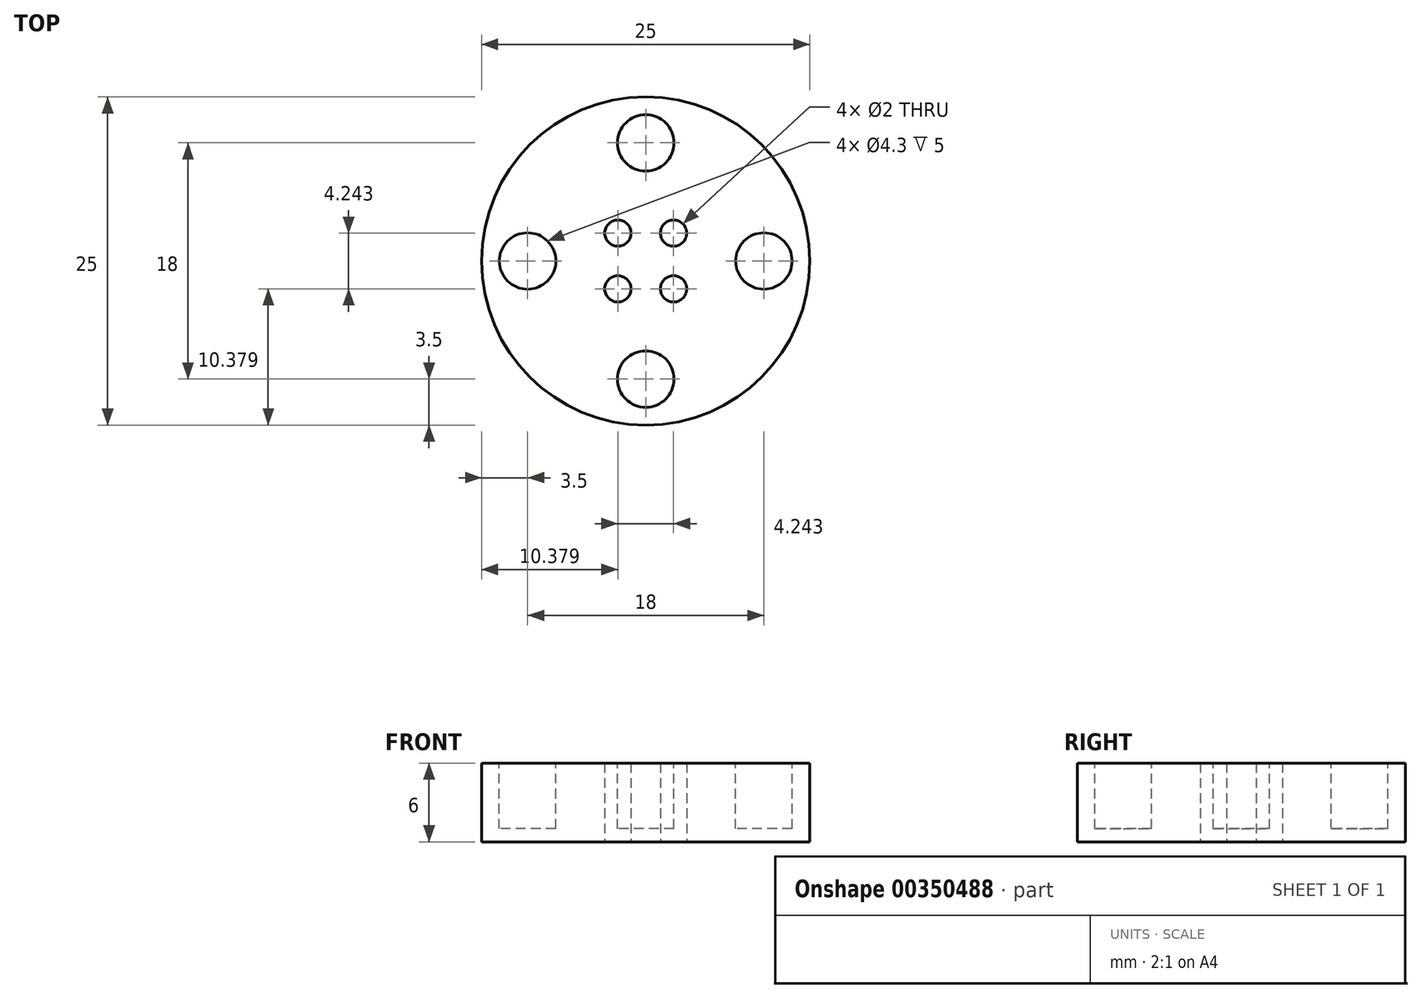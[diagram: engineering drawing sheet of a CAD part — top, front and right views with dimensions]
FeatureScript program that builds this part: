
annotation { "Feature Type Name" : "Feature", "Feature Type Description" : "" }
export const myFeature = defineFeature(function(context is Context, id is Id, definition is map)
    precondition{}
    {
        {
            var Q0;
            Q0=qCreatedBy(makeId("Top.planeOp"),FACE);
            var sketch = newSketch(context, id + "F0", { "sketchPlane" : qUnion([Q0])});
            skCircle(sketch, "E0", {"center": v(0, 0) * mm, "radius": 12.5 * mm});
            skCircle(sketch, "E1", {"center": v(2.12, 2.12) * mm, "radius": 1 * mm});
            skCircle(sketch, "E2.1.0", {"center": v(-2.12, 2.12) * mm, "radius": 1 * mm});
            skCircle(sketch, "E2.2.0", {"center": v(-2.12, -2.12) * mm, "radius": 1 * mm});
            skCircle(sketch, "E2.3.0", {"center": v(2.12, -2.12) * mm, "radius": 1 * mm});
            skSolve(sketch);
        }
        {
            var Q0;
            Q0 = qSketchRegion(id + "F0", true);
            extrude(context, id + "F1", {"entities" : qUnion([Q0]), "depth" : 6 * mm});
        }
        {
            var Q0;
            Q0=makeQuery(id+"F1.opExtrude","CAP_FACE",FACE,{"disambiguationData":[OSD([sQuery(id+"F0.wireOp",EDGE,"E0"),sQuery(id+"F0.wireOp",EDGE,"E1"),sQuery(id+"F0.wireOp",EDGE,"E2.1.0"),sQuery(id+"F0.wireOp",EDGE,"E2.2.0"),sQuery(id+"F0.wireOp",EDGE,"E2.3.0")])],"isStart":false});
            var sketch = newSketch(context, id + "F2", { "sketchPlane" : qUnion([Q0])});
            skLineSegment(sketch, "E3", {"start": v(0, 9) * mm, "end": v(0, 0) * mm});
            skLineSegment(sketch, "E4", {"start": v(0, 0) * mm, "end": v(10.37, 0) * mm});
            skCircle(sketch, "E5", {"center": v(0, 9) * mm, "radius": 2.15 * mm});
            skCircle(sketch, "E6.1.0", {"center": v(9, 0) * mm, "radius": 2.15 * mm});
            skCircle(sketch, "E6.2.0", {"center": v(0, -9) * mm, "radius": 2.15 * mm});
            skCircle(sketch, "E6.3.0", {"center": v(-9, 0) * mm, "radius": 2.15 * mm});
            skPoint(sketch, "E6.center", {"position": v(0, 0) * mm});
            skLineSegment(sketch, "E6.anchor1", {"start": v(0, 0) * mm, "end": v(0, 9) * mm, "construction": true});
            skLineSegment(sketch, "E6.anchor2", {"start": v(0, 0) * mm, "end": v(-9, 0) * mm, "construction": true});
            skSolve(sketch);
        }
        {
            var Q0;
            Q0 = qSketchRegion(id + "F2", true);
            extrude(context, id + "F3", {"entities" : qUnion([Q0]), "operationType" : NewBodyOperationType.REMOVE, "oppositeDirection" : true, "depth" : 5 * mm});
        }
    });
